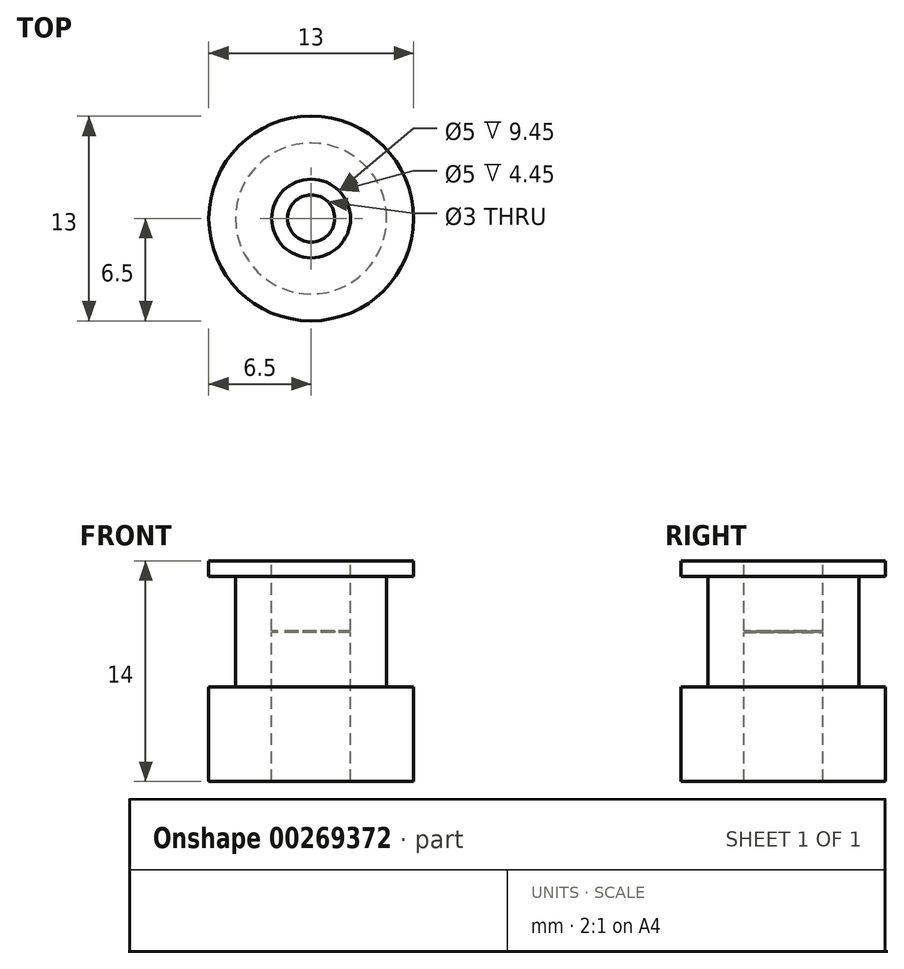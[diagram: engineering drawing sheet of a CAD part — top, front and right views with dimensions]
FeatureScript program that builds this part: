
annotation { "Feature Type Name" : "Feature", "Feature Type Description" : "" }
export const myFeature = defineFeature(function(context is Context, id is Id, definition is map)
    precondition{}
    {
        {
            var Q0;
            Q0=qCreatedBy(makeId("Top.planeOp"),FACE);
            var sketch = newSketch(context, id + "F0", { "sketchPlane" : qUnion([Q0])});
            skCircle(sketch, "E0", {"center": v(0, 0) * mm, "radius": 6.5 * mm});
            skSolve(sketch);
        }
        {
            var Q0;
            Q0=makeQuery(id+"F0.imprint","IMPRINT",FACE,{"disambiguationData":[TD([[makeQuery(id+"F0.imprint","IMPRINT",EDGE,{"derivedFrom":sQuery(id+"F0.wireOp",EDGE,"E0")}),1.0]])]});
            extrude(context, id + "F1", {"entities" : qUnion([Q0]), "depth" : 6 * mm});
        }
        {
            var Q0;
            Q0=makeQuery(id+"F1.opExtrude","CAP_FACE",FACE,{"disambiguationData":[OSD([sQuery(id+"F0.wireOp",EDGE,"E0")])],"isStart":false});
            var sketch = newSketch(context, id + "F2", { "sketchPlane" : qUnion([Q0])});
            skCircle(sketch, "E1", {"center": v(0, 0) * mm, "radius": 4.8 * mm});
            skSolve(sketch);
        }
        {
            var Q0;
            Q0=makeQuery(id+"F2.imprint","IMPRINT",FACE,{"disambiguationData":[TD([[makeQuery(id+"F2.imprint","IMPRINT",EDGE,{"derivedFrom":sQuery(id+"F2.wireOp",EDGE,"E1")}),1.0]])]});
            extrude(context, id + "F3", {"entities" : qUnion([Q0]), "operationType" : NewBodyOperationType.ADD, "depth" : 7 * mm});
        }
        {
            var Q0;
            Q0=makeQuery(id+"F3.opExtrude","CAP_FACE",FACE,{"disambiguationData":[OSD([sQuery(id+"F2.wireOp",EDGE,"E1")])],"isStart":false});
            var sketch = newSketch(context, id + "F4", { "sketchPlane" : qUnion([Q0])});
            skCircle(sketch, "E2.0", {"center": v(0, 0) * mm, "radius": 6.5 * mm});
            skSolve(sketch);
        }
        {
            var Q0;
            Q0=makeQuery(id+"F4.imprint","IMPRINT",FACE,{"disambiguationData":[TD([[makeQuery(id+"F4.imprint","IMPRINT",EDGE,{"derivedFrom":makeQuery(id+"F3.opExtrude","CAP_EDGE",EDGE,{"disambiguationData":[OSD([sQuery(id+"F2.wireOp",EDGE,"E1")])],"isStart":false})}),1.0]])]});
            var Q1;
            Q1=makeQuery(id+"F4.imprint","IMPRINT",FACE,{"disambiguationData":[TD([[makeQuery(id+"F4.imprint","IMPRINT",EDGE,{"derivedFrom":sQuery(id+"F4.wireOp",EDGE,"E2.0")}),1.0]])]});
            extrude(context, id + "F5", {"entities" : qUnion([Q0, Q1]), "operationType" : NewBodyOperationType.ADD, "depth" : 1 * mm});
        }
        {
            var Q0;
            Q0=makeQuery(id+"F5.opExtrude","CAP_FACE",FACE,{"disambiguationData":[OSD([sQuery(id+"F4.wireOp",EDGE,"E2.0")])],"isStart":false});
            var sketch = newSketch(context, id + "F6", { "sketchPlane" : qUnion([Q0])});
            skCircle(sketch, "E3", {"center": v(0, 0) * mm, "radius": 2.5 * mm});
            skSolve(sketch);
        }
        {
            var Q0;
            Q0=makeQuery(id+"F6.imprint","IMPRINT",FACE,{"disambiguationData":[TD([[makeQuery(id+"F6.imprint","IMPRINT",EDGE,{"derivedFrom":sQuery(id+"F6.wireOp",EDGE,"E3")}),1.0]])]});
            extrude(context, id + "F7", {"entities" : qUnion([Q0]), "operationType" : NewBodyOperationType.REMOVE, "endBound" : BoundingType.THROUGH_ALL, "oppositeDirection" : true, "depth" : 25 * mm});
        }
        {
            var Q0;
            Q0=makeQuery(id+"F1.opExtrude","CAP_FACE",FACE,{"disambiguationData":[OSD([sQuery(id+"F0.wireOp",EDGE,"E0")])],"isStart":false});
            var Q1;
            Q1=makeQuery(id+"F5.opExtrude","CAP_FACE",FACE,{"disambiguationData":[OSD([sQuery(id+"F4.wireOp",EDGE,"E2.0")])],"isStart":true});
            cPlane(context, id + "F8", {"entities" : qUnion([Q0, Q1]), "cplaneType" : CPlaneType.MID_PLANE, "offset" : 25 * mm, "width" : 150 * mm, "height" : 150 * mm});
        }
        {
            var Q0;
            Q0=qCreatedBy(id+"F8.planeOp",FACE);
            var sketch = newSketch(context, id + "F9", { "sketchPlane" : qUnion([Q0])});
            skCircle(sketch, "E4", {"center": v(0, 0) * mm, "radius": 4.8 * mm});
            skCircle(sketch, "E5.0", {"center": v(0, 0) * mm, "radius": 4.9 * mm});
            skCircle(sketch, "E6.0", {"center": v(0, 0) * mm, "radius": 1.5 * mm});
            skSolve(sketch);
        }
        {
            var Q0;
            Q0=makeQuery(id+"F9.imprint","IMPRINT",FACE,{"disambiguationData":[TD([[makeQuery(id+"F9.imprint","IMPRINT",EDGE,{"derivedFrom":sQuery(id+"F9.wireOp",EDGE,"E4")}),1.0]])]});
            extrude(context, id + "F10", {"entities" : qUnion([Q0]), "operationType" : NewBodyOperationType.ADD, "endBound" : BoundingType.SYMMETRIC, "depth" : 0.1 * mm, "offsetDistance" : 25 * mm});
        }
    });
